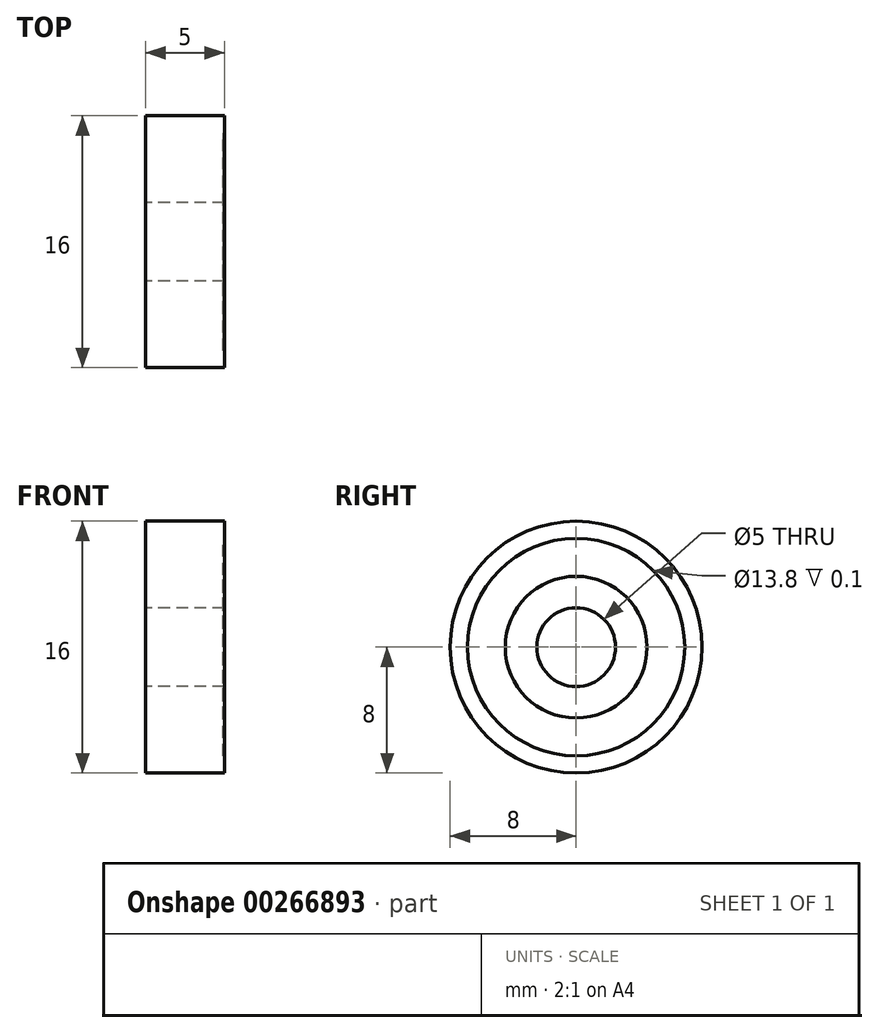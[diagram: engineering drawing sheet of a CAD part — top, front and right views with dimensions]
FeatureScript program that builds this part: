
annotation { "Feature Type Name" : "Feature", "Feature Type Description" : "" }
export const myFeature = defineFeature(function(context is Context, id is Id, definition is map)
    precondition{}
    {
        {
            var Q0;
            Q0=qCreatedBy(makeId("Right.planeOp"),FACE);
            var sketch = newSketch(context, id + "F0", { "sketchPlane" : qUnion([Q0])});
            skCircle(sketch, "E0", {"center": v(0, 0) * mm, "radius": 8 * mm});
            skCircle(sketch, "E1", {"center": v(0, 0) * mm, "radius": 2.5 * mm});
            skSolve(sketch);
        }
        {
            var Q0;
            Q0 = qSketchRegion(id + "F0", true);
            extrude(context, id + "F1", {"entities" : qUnion([Q0]), "depth" : 2.5 * mm, "hasSecondDirection" : true, "secondDirectionOppositeDirection" : true, "secondDirectionDepth" : 2.5 * mm});
        }
        {
            var Q0;
            Q0=makeQuery(id+"F1.opExtrude","CAP_FACE",FACE,{"disambiguationData":[OSD([sQuery(id+"F0.wireOp",EDGE,"E0"),sQuery(id+"F0.wireOp",EDGE,"E1")])],"isStart":false});
            var sketch = newSketch(context, id + "F2", { "sketchPlane" : qUnion([Q0])});
            skCircle(sketch, "E2", {"center": v(0, 0) * mm, "radius": 4.5 * mm});
            skCircle(sketch, "E3", {"center": v(0, 0) * mm, "radius": 6.9 * mm});
            skSolve(sketch);
        }
        {
            var Q0;
            Q0 = qSketchRegion(id + "F2", true);
            extrude(context, id + "F3", {"entities" : qUnion([Q0]), "operationType" : NewBodyOperationType.REMOVE, "oppositeDirection" : true, "depth" : 0.1 * mm});
        }
    });
